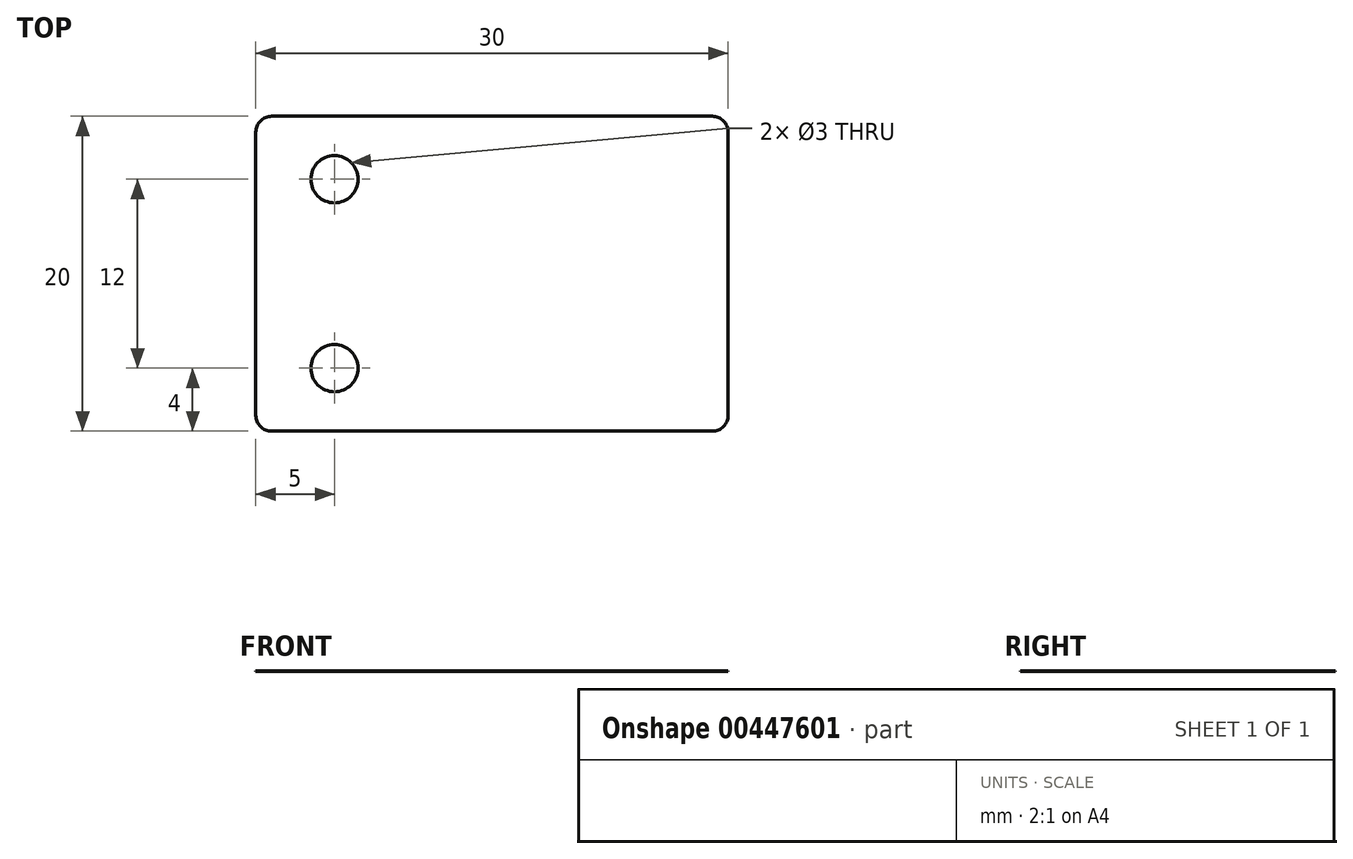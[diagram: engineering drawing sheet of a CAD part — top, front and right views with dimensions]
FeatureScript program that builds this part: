
annotation { "Feature Type Name" : "Feature", "Feature Type Description" : "" }
export const myFeature = defineFeature(function(context is Context, id is Id, definition is map)
    precondition{}
    {
        {
            var Q0;
            Q0=qCreatedBy(makeId("Top.planeOp"),FACE);
            var sketch = newSketch(context, id + "F0", { "sketchPlane" : qUnion([Q0])});
            skLineSegment(sketch, "E0.bottom", {"start": v(0, 0) * mm, "end": v(30, 0) * mm});
            skLineSegment(sketch, "E0.top", {"start": v(0, 20) * mm, "end": v(30, 20) * mm});
            skLineSegment(sketch, "E0.left", {"start": v(0, 0) * mm, "end": v(0, 20) * mm});
            skLineSegment(sketch, "E0.right", {"start": v(30, 0) * mm, "end": v(30, 20) * mm});
            skSolve(sketch);
        }
        {
            var Q0;
            Q0=makeQuery(id+"F0.imprint","IMPRINT",FACE,{"disambiguationData":[TD([[makeQuery(id+"F0.imprint","IMPRINT",EDGE,{"derivedFrom":sQuery(id+"F0.wireOp",EDGE,"E0.bottom")}),1.0]])]});
            extrude(context, id + "F1", {"entities" : qUnion([Q0]), "depth" : 1 / 203.2 * mm});
        }
        {
            var Q0;
            Q0=makeQuery(id+"F1.opExtrude","CAP_FACE",FACE,{"disambiguationData":[OSD([sQuery(id+"F0.wireOp",EDGE,"E0.bottom"),sQuery(id+"F0.wireOp",EDGE,"E0.top"),sQuery(id+"F0.wireOp",EDGE,"E0.left"),sQuery(id+"F0.wireOp",EDGE,"E0.right")])],"isStart":false});
            var sketch = newSketch(context, id + "F2", { "sketchPlane" : qUnion([Q0])});
            skCircle(sketch, "E1", {"center": v(5, 16) * mm, "radius": 1.5 * mm});
            skCircle(sketch, "E2", {"center": v(5, 4) * mm, "radius": 1.5 * mm});
            skLineSegment(sketch, "E3", {"start": v(5, 16) * mm, "end": v(5, 20) * mm, "construction": true});
            skLineSegment(sketch, "E4", {"start": v(5, 4) * mm, "end": v(5, 0) * mm, "construction": true});
            skSolve(sketch);
        }
        {
            var Q0;
            Q0 = qSketchRegion(id + "F2", true);
            extrude(context, id + "F3", {"entities" : qUnion([Q0]), "operationType" : NewBodyOperationType.REMOVE, "oppositeDirection" : true, "depth" : 25 * mm});
        }
        {
            var Q0;
            Q0=makeQuery(id+"F1.opExtrude","SWEPT_EDGE",EDGE,{"disambiguationData":[OSD([sQuery(id+"F0.wireOp",EDGE,"E0.top"),sQuery(id+"F0.wireOp",EDGE,"E0.left")])]});
            var Q1;
            Q1=makeQuery(id+"F1.opExtrude","SWEPT_EDGE",EDGE,{"disambiguationData":[OSD([sQuery(id+"F0.wireOp",EDGE,"E0.top"),sQuery(id+"F0.wireOp",EDGE,"E0.right")])]});
            var Q2;
            Q2=makeQuery(id+"F1.opExtrude","SWEPT_EDGE",EDGE,{"disambiguationData":[OSD([sQuery(id+"F0.wireOp",EDGE,"E0.bottom"),sQuery(id+"F0.wireOp",EDGE,"E0.right")])]});
            var Q3;
            Q3=makeQuery(id+"F1.opExtrude","SWEPT_EDGE",EDGE,{"disambiguationData":[OSD([sQuery(id+"F0.wireOp",EDGE,"E0.bottom"),sQuery(id+"F0.wireOp",EDGE,"E0.left")])]});
            fillet(context, id + "F4", {"entities" : qUnion([Q0, Q1, Q2, Q3]), "radius" : 1 * mm, "tangentPropagation" : true, "allowEdgeOverflow" : false});
        }
    });
